# Revit family: Board & Batten
name_source: partatom
category: Generic Models
revit_build: Autodesk Revit 2017 (Build: 20160225_1515(x64)
units: mm (PartAtom-declared; Revit-internal decimal feet)

## family parameters
Always vertical = No
Can host rebar = No
Cut with Voids When Loaded = No
Part Type = Normal
Room Calculation Point = No
Round Connector Dimension = Use Diameter
Shared = No
Work Plane-Based = Yes

## types (1)
- Board & Batten
    Batten Spacing = 0' - 5"
    Default Elevation = 4' - 0"
    Manufacturer = New Horizon Shutters
    Model = Board & Batten
    Panel_Width = 1' - 6"
    Shutter Apperance = Default
    Shutter Height = 5' - 4"
    Shutter Thickness = 0' - 1 1/4"
    Type Comments = **** All shutter dimensions and configurations to be approved by NHSI ****
    URL = www.newhorizonshutters.com
    Visibility Of Batten = No
    Visibility Of Center Batten = No
    Visibility Of Crossbuck = No
    Visibility Of Crossbuck mirrored = No
    batten size = 0' - 5"
    number of v grooves = 4

## geometry (parser evidence)
native form markers: Sweep x2
no freeform markers — native parametric forms only
